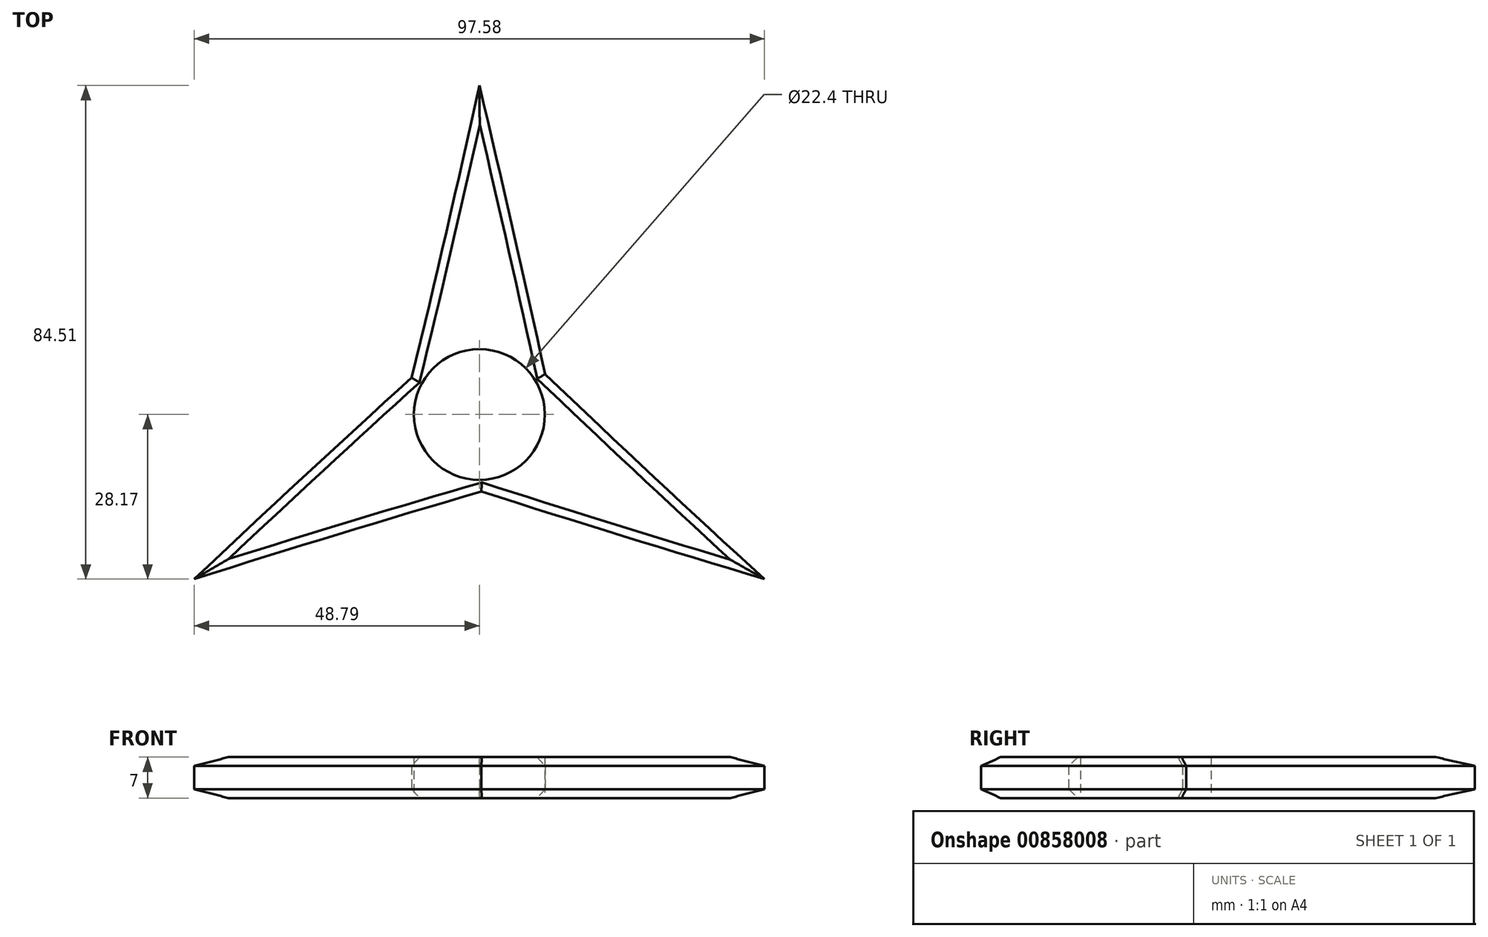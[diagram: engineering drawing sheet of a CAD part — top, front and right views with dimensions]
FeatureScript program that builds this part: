
annotation { "Feature Type Name" : "Feature", "Feature Type Description" : "" }
export const myFeature = defineFeature(function(context is Context, id is Id, definition is map)
    precondition{}
    {
        {
            var Q0;
            Q0=qCreatedBy(makeId("Top.planeOp"),FACE);
            var sketch = newSketch(context, id + "F0", { "sketchPlane" : qUnion([Q0])});
            skCircle(sketch, "E0", {"center": v(0, 0) * mm, "radius": 11.2 * mm});
            skCircle(sketch, "E1", {"center": v(0, 0) * mm, "radius": 13.2 * mm});
            skArc(sketch, "E2", {"start": v(-11.6, 6.3) * mm, "mid": v(-5.65, 31.28) * mm, "end": v(0, 56.34) * mm});
            skArc(sketch, "E3.1.0", {"start": v(0.35, -13.2) * mm, "mid": v(-24.27, -20.54) * mm, "end": v(-48.8, -28.17) * mm});
            skArc(sketch, "E3.2.0", {"start": v(11.25, 6.9) * mm, "mid": v(29.92, -10.75) * mm, "end": v(48.8, -28.17) * mm});
            skArc(sketch, "E4", {"start": v(11.25, 6.9) * mm, "mid": v(5.74, 31.65) * mm, "end": v(0, 56.34) * mm});
            skArc(sketch, "E5.1.0", {"start": v(-11.6, 6.3) * mm, "mid": v(-30.28, -10.85) * mm, "end": v(-48.8, -28.17) * mm});
            skArc(sketch, "E5.2.0", {"start": v(0.35, -13.2) * mm, "mid": v(24.54, -20.8) * mm, "end": v(48.8, -28.17) * mm});
            skLineSegment(sketch, "E6", {"start": v(0, 56.34) * mm, "end": v(0, 13.2) * mm});
            skLineSegment(sketch, "E7", {"start": v(-48.8, -28.17) * mm, "end": v(-11.05, -7.22) * mm});
            skLineSegment(sketch, "E8", {"start": v(48.8, -28.17) * mm, "end": v(11.25, -6.9) * mm});
            skLineSegment(sketch, "E9", {"start": v(11.25, -6.9) * mm, "end": v(36.53, -21.22) * mm});
            skSolve(sketch);
        }
        {
            var Q0;
            {var subQ0=sQuery(id+"F0.wireOp",EDGE,"E4");Q0=makeQuery(id+"F0.imprint","IMPRINT",FACE,{"disambiguationData":[TD([[makeQuery(id+"F0.imprint","IMPRINT",EDGE,{"derivedFrom":subQ0}),1.0]])]});}
            var Q1;
            {var subQ0=sQuery(id+"F0.wireOp",EDGE,"E2");Q1=makeQuery(id+"F0.imprint","IMPRINT",FACE,{"disambiguationData":[TD([[makeQuery(id+"F0.imprint","IMPRINT",EDGE,{"derivedFrom":subQ0}),-1.0]])]});}
            var Q2;
            Q2=makeQuery(id+"F0.imprint","IMPRINT",FACE,{"disambiguationData":[TD([[makeQuery(id+"F0.imprint","IMPRINT",EDGE,{"derivedFrom":sQuery(id+"F0.wireOp",EDGE,"E0")}),-1.0]])]});
            var Q3;
            {var subQ0=sQuery(id+"F0.wireOp",EDGE,"E3.2.0");Q3=makeQuery(id+"F0.imprint","IMPRINT",FACE,{"disambiguationData":[TD([[makeQuery(id+"F0.imprint","IMPRINT",EDGE,{"derivedFrom":subQ0}),-1.0]])]});}
            var Q4;
            {var subQ0=sQuery(id+"F0.wireOp",EDGE,"E5.2.0");Q4=makeQuery(id+"F0.imprint","IMPRINT",FACE,{"disambiguationData":[TD([[makeQuery(id+"F0.imprint","IMPRINT",EDGE,{"derivedFrom":subQ0}),1.0]])]});}
            var Q5;
            {var subQ0=sQuery(id+"F0.wireOp",EDGE,"E3.1.0");Q5=makeQuery(id+"F0.imprint","IMPRINT",FACE,{"disambiguationData":[TD([[makeQuery(id+"F0.imprint","IMPRINT",EDGE,{"derivedFrom":subQ0}),-1.0]])]});}
            var Q6;
            {var subQ0=sQuery(id+"F0.wireOp",EDGE,"E5.1.0");Q6=makeQuery(id+"F0.imprint","IMPRINT",FACE,{"disambiguationData":[TD([[makeQuery(id+"F0.imprint","IMPRINT",EDGE,{"derivedFrom":subQ0}),1.0]])]});}
            extrude(context, id + "F1", {"entities" : qUnion([Q0, Q1, Q2, Q3, Q4, Q5, Q6]), "depth" : 7 * mm, "offsetDistance" : 25 * mm});
        }
        {
            var Q0;
            Q0=makeQuery(id+"F1.opExtrude","CAP_EDGE",EDGE,{"disambiguationData":[OSD([sQuery(id+"F0.wireOp",EDGE,"E3.1.0")])],"isStart":false});
            var Q1;
            Q1=makeQuery(id+"F1.opExtrude","CAP_EDGE",EDGE,{"disambiguationData":[OSD([sQuery(id+"F0.wireOp",EDGE,"E5.1.0")])],"isStart":false});
            var Q2;
            Q2=makeQuery(id+"F1.opExtrude","CAP_EDGE",EDGE,{"disambiguationData":[OSD([sQuery(id+"F0.wireOp",EDGE,"E2")])],"isStart":false});
            var Q3;
            Q3=makeQuery(id+"F1.opExtrude","CAP_EDGE",EDGE,{"disambiguationData":[OSD([sQuery(id+"F0.wireOp",EDGE,"E4")])],"isStart":false});
            var Q4;
            Q4=makeQuery(id+"F1.opExtrude","CAP_EDGE",EDGE,{"disambiguationData":[OSD([sQuery(id+"F0.wireOp",EDGE,"E3.2.0")])],"isStart":false});
            var Q5;
            Q5=makeQuery(id+"F1.opExtrude","CAP_EDGE",EDGE,{"disambiguationData":[OSD([sQuery(id+"F0.wireOp",EDGE,"E5.2.0")])],"isStart":false});
            var Q6;
            Q6=makeQuery(id+"F1.opExtrude","CAP_EDGE",EDGE,{"disambiguationData":[OSD([sQuery(id+"F0.wireOp",EDGE,"E5.2.0")])],"isStart":true});
            var Q7;
            Q7=makeQuery(id+"F1.opExtrude","CAP_EDGE",EDGE,{"disambiguationData":[OSD([sQuery(id+"F0.wireOp",EDGE,"E3.2.0")])],"isStart":true});
            var Q8;
            Q8=makeQuery(id+"F1.opExtrude","CAP_EDGE",EDGE,{"disambiguationData":[OSD([sQuery(id+"F0.wireOp",EDGE,"E2")])],"isStart":true});
            var Q9;
            Q9=makeQuery(id+"F1.opExtrude","CAP_EDGE",EDGE,{"disambiguationData":[OSD([sQuery(id+"F0.wireOp",EDGE,"E4")])],"isStart":true});
            var Q10;
            Q10=makeQuery(id+"F1.opExtrude","CAP_EDGE",EDGE,{"disambiguationData":[OSD([sQuery(id+"F0.wireOp",EDGE,"E5.1.0")])],"isStart":true});
            var Q11;
            Q11=makeQuery(id+"F1.opExtrude","CAP_EDGE",EDGE,{"disambiguationData":[OSD([sQuery(id+"F0.wireOp",EDGE,"E3.1.0")])],"isStart":true});
            chamfer(context, id + "F2", {"entities" : qUnion([Q0, Q1, Q2, Q3, Q4, Q5, Q6, Q7, Q8, Q9, Q10, Q11]), "width" : 1.5 * mm, "tangentPropagation" : true});
        }
    });
